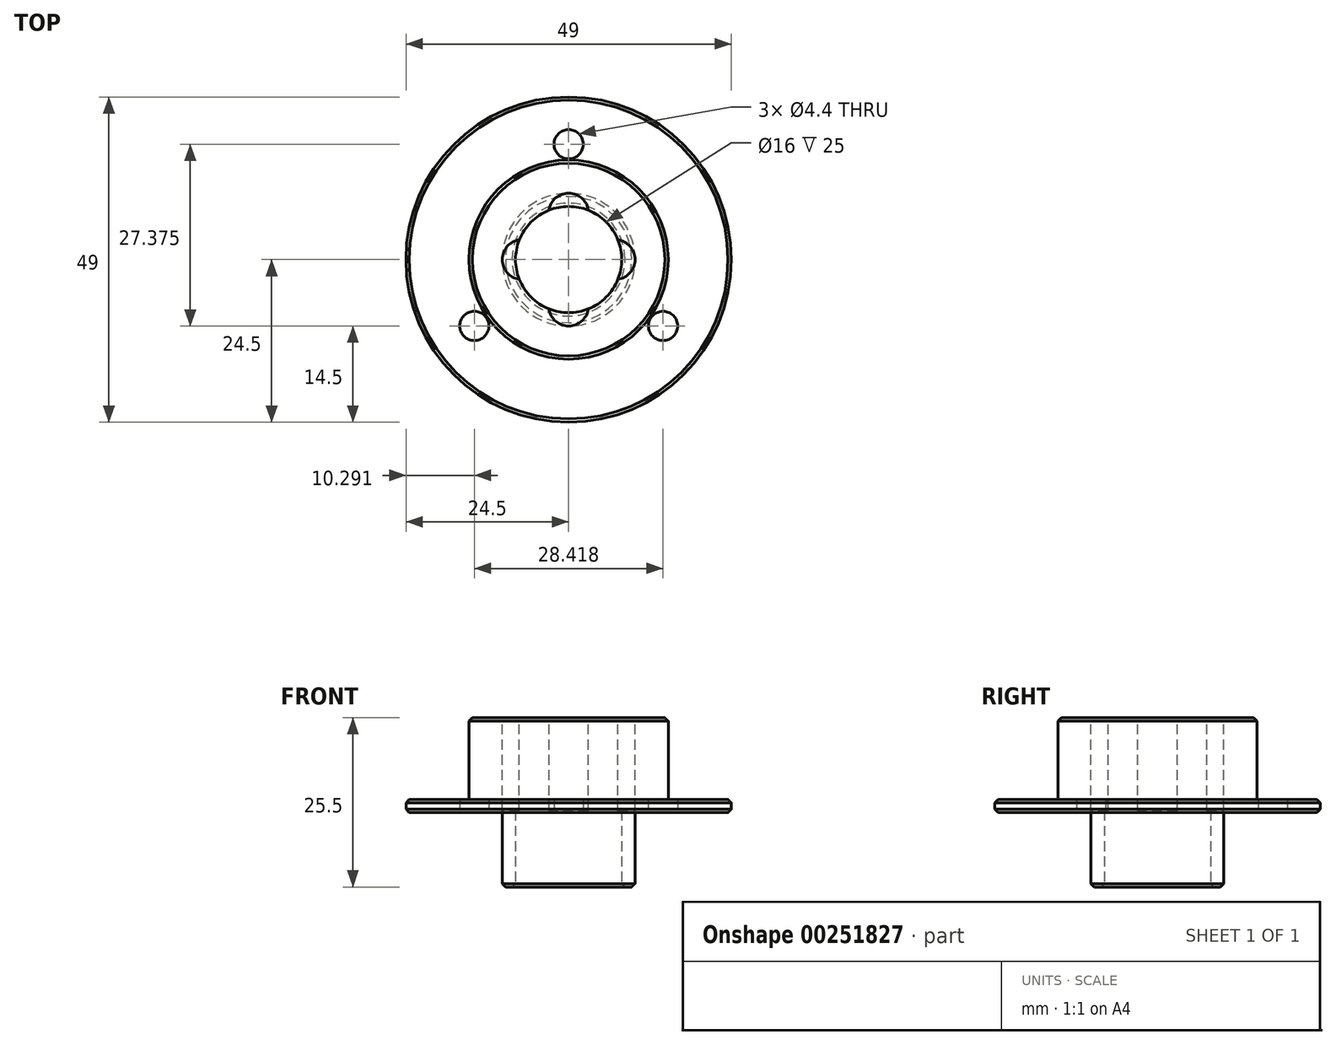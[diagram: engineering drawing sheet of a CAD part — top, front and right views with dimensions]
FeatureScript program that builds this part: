
annotation { "Feature Type Name" : "Feature", "Feature Type Description" : "" }
export const myFeature = defineFeature(function(context is Context, id is Id, definition is map)
    precondition{}
    {
        {
            var Q0;
            Q0=qCreatedBy(makeId("Top.planeOp"),FACE);
            var sketch = newSketch(context, id + "F0", { "sketchPlane" : qUnion([Q0])});
            skCircle(sketch, "E0", {"center": v(0, 0) * mm, "radius": 24.5 * mm});
            skCircle(sketch, "E1", {"center": v(0, 0) * mm, "radius": 15 * mm});
            skLineSegment(sketch, "E2", {"start": v(0, 33.29) * mm, "end": v(0, -23.13) * mm, "construction": true});
            skCircle(sketch, "E3", {"center": v(0, 0) * mm, "radius": 8 * mm});
            skLineSegment(sketch, "E4", {"start": v(-31.07, 0) * mm, "end": v(33.2, 0) * mm, "construction": true});
            skCircle(sketch, "E5", {"center": v(0, 0) * mm, "radius": 17.38 * mm, "construction": true});
            skLineSegment(sketch, "E6", {"start": v(-18.82, -10) * mm, "end": v(18.86, -10) * mm, "construction": true});
            skCircle(sketch, "E7", {"center": v(0, 0) * mm, "radius": 7 * mm, "construction": true});
            skCircle(sketch, "E8", {"center": v(0, 0) * mm, "radius": 10 * mm});
            skPoint(sketch, "E9", {"position": v(0, 17.38) * mm});
            skPoint(sketch, "E10", {"position": v(14.2, -10) * mm});
            skPoint(sketch, "E11", {"position": v(-14.2, -10) * mm});
            skPoint(sketch, "E12", {"position": v(0, 7) * mm});
            skPoint(sketch, "E13", {"position": v(7, 0) * mm});
            skPoint(sketch, "E14", {"position": v(0, -7) * mm});
            skPoint(sketch, "E15", {"position": v(-7, 0) * mm});
            skSolve(sketch);
        }
        {
            var Q0;
            Q0=makeQuery(id+"F0.imprint","IMPRINT",FACE,{"disambiguationData":[TD([[makeQuery(id+"F0.imprint","IMPRINT",EDGE,{"derivedFrom":sQuery(id+"F0.wireOp",EDGE,"E0")}),1.0]])]});
            var Q1;
            Q1=makeQuery(id+"F0.imprint","IMPRINT",FACE,{"disambiguationData":[TD([[makeQuery(id+"F0.imprint","IMPRINT",EDGE,{"derivedFrom":sQuery(id+"F0.wireOp",EDGE,"E1")}),1.0]])]});
            extrude(context, id + "F1", {"entities" : qUnion([Q0, Q1]), "depth" : 2 * mm});
        }
        {
            var Q0;
            Q0=makeQuery(id+"F1.opExtrude","CAP_FACE",FACE,{"disambiguationData":[OSD([sQuery(id+"F0.wireOp",EDGE,"E0"),sQuery(id+"F0.wireOp",EDGE,"E8")])],"isStart":false});
            var sketch = newSketch(context, id + "F2", { "sketchPlane" : qUnion([Q0])});
            skCircle(sketch, "E16.0", {"center": v(0, 0) * mm, "radius": 15 * mm});
            skCircle(sketch, "E17.0", {"center": v(0, 0) * mm, "radius": 8 * mm});
            skSolve(sketch);
        }
        {
            var Q0;
            Q0 = qSketchRegion(id + "F2", true);
            extrude(context, id + "F3", {"entities" : qUnion([Q0]), "operationType" : NewBodyOperationType.ADD, "depth" : 12.3 * mm});
        }
        {
            var Q0;
            Q0=makeQuery(id+"F1.opExtrude","CAP_FACE",FACE,{"disambiguationData":[OSD([sQuery(id+"F0.wireOp",EDGE,"E0"),sQuery(id+"F0.wireOp",EDGE,"E8")])],"isStart":false});
            var sketch = newSketch(context, id + "F4", { "sketchPlane" : qUnion([Q0])});
            skCircle(sketch, "E18.0", {"center": v(0, 0) * mm, "radius": 10 * mm});
            skCircle(sketch, "E19.0", {"center": v(0, 0) * mm, "radius": 8 * mm});
            skSolve(sketch);
        }
        {
            var Q0;
            Q0 = qSketchRegion(id + "F4", true);
            extrude(context, id + "F5", {"entities" : qUnion([Q0]), "operationType" : NewBodyOperationType.ADD, "oppositeDirection" : true, "depth" : 13.2 * mm});
        }
        {
            var Q0;
            Q0=sQuery(id+"F0.wireOp",VERTEX,"E9");
            var Q1;
            Q1=sQuery(id+"F0.wireOp",VERTEX,"E11");
            var Q2;
            Q2=sQuery(id+"F0.wireOp",VERTEX,"E10");
            var Q3;
            Q3=makeQuery(id+"F1.opExtrude","SWEPT_BODY",BODY,{"disambiguationData":[OSD([sQuery(id+"F0.wireOp",EDGE,"E0"),sQuery(id+"F0.wireOp",EDGE,"E8")])]});
            hole(context, id + "F6", {"style" : HoleStyle.SIMPLE, "endStyle" : HoleEndStyle.BLIND, "oppositeDirection" : true, "standardTappedOrClearance" : lookupTablePath({ "standard" : "ISO", "fit" : "Normal", "size" : "M4", "type" : "Clearance" }), "standardBlindInLast" : lookupTablePath({ "fit" : "Standard", "standard" : "ISO", "size" : "M4", "type" : "Clearance" }), "holeDiameter" : 4.4 * mm, "holeDepth" : 14 * mm, "tappedDepth" : 12 * mm, "tapClearance" : 3, "locations" : qUnion([Q0, Q1, Q2]), "scope" : qUnion([Q3])});
        }
        {
            var Q0;
            Q0=makeQuery(id+"F3.opExtrude","CAP_FACE",FACE,{"disambiguationData":[OSD([sQuery(id+"F2.wireOp",EDGE,"E16.0"),sQuery(id+"F2.wireOp",EDGE,"E17.0")])],"isStart":false});
            var sketch = newSketch(context, id + "F7", { "sketchPlane" : qUnion([Q0])});
            skPoint(sketch, "E20.0", {"position": v(0, 7) * mm});
            skPoint(sketch, "E21.0", {"position": v(-7, 0) * mm});
            skPoint(sketch, "E22.0", {"position": v(7, 0) * mm});
            skPoint(sketch, "E23.0", {"position": v(0, -7) * mm});
            skCircle(sketch, "E24", {"center": v(0, 7) * mm, "radius": 3 * mm});
            skCircle(sketch, "E25", {"center": v(-7, 0) * mm, "radius": 3 * mm});
            skCircle(sketch, "E26", {"center": v(7, 0) * mm, "radius": 3 * mm});
            skCircle(sketch, "E27", {"center": v(0, -7) * mm, "radius": 3 * mm});
            skSolve(sketch);
        }
        {
            var Q0;
            Q0 = qSketchRegion(id + "F7", true);
            extrude(context, id + "F8", {"entities" : qUnion([Q0]), "operationType" : NewBodyOperationType.REMOVE, "oppositeDirection" : true, "depth" : 14 * mm});
        }
        {
            var Q0;
            Q0=makeQuery(id+"F8.boolean.opBoolean","COPY",EDGE,{"derivedFrom":makeQuery(id+"F8.opExtrude","CAP_EDGE",EDGE,{"disambiguationData":[OSD([sQuery(id+"F7.wireOp",EDGE,"E25")])],"isStart":true})});
            var Q1;
            Q1=makeQuery(id+"F8.boolean.opBoolean","COPY",EDGE,{"derivedFrom":makeQuery(id+"F8.opExtrude","CAP_EDGE",EDGE,{"disambiguationData":[OSD([sQuery(id+"F7.wireOp",EDGE,"E24")])],"isStart":true})});
            var Q2;
            Q2=makeQuery(id+"F8.boolean.opBoolean","COPY",EDGE,{"derivedFrom":makeQuery(id+"F8.opExtrude","CAP_EDGE",EDGE,{"disambiguationData":[OSD([sQuery(id+"F7.wireOp",EDGE,"E26")])],"isStart":true})});
            var Q3;
            Q3=makeQuery(id+"F8.boolean.opBoolean","COPY",EDGE,{"derivedFrom":makeQuery(id+"F8.opExtrude","CAP_EDGE",EDGE,{"disambiguationData":[OSD([sQuery(id+"F7.wireOp",EDGE,"E27")])],"isStart":true})});
            var Q4;
            Q4=makeQuery(id+"F3.opExtrude","CAP_EDGE",EDGE,{"disambiguationData":[OSD([sQuery(id+"F2.wireOp",EDGE,"E16.0")])],"isStart":false});
            var Q5;
            Q5=makeQuery(id+"F1.opExtrude","CAP_EDGE",EDGE,{"disambiguationData":[OSD([sQuery(id+"F0.wireOp",EDGE,"E0")])],"isStart":false});
            var Q6;
            Q6=makeQuery(id+"F5.opExtrude","CAP_EDGE",EDGE,{"disambiguationData":[OSD([sQuery(id+"F4.wireOp",EDGE,"E18.0")])],"isStart":false});
            var Q7;
            Q7=makeQuery(id+"F5.opExtrude","CAP_EDGE",EDGE,{"disambiguationData":[OSD([sQuery(id+"F4.wireOp",EDGE,"E19.0")])],"isStart":false});
            chamfer(context, id + "F9", {"entities" : qUnion([Q0, Q1, Q2, Q3, Q4, Q5, Q6, Q7]), "width" : .5 * mm, "tangentPropagation" : true});
        }
        {
            var Q0;
            Q0=makeQuery(id+"F1.opExtrude","CAP_EDGE",EDGE,{"disambiguationData":[OSD([sQuery(id+"F0.wireOp",EDGE,"E0")])],"isStart":true});
            chamfer(context, id + "F10", {"entities" : qUnion([Q0]), "width" : .5 * mm, "tangentPropagation" : true});
        }
    });
